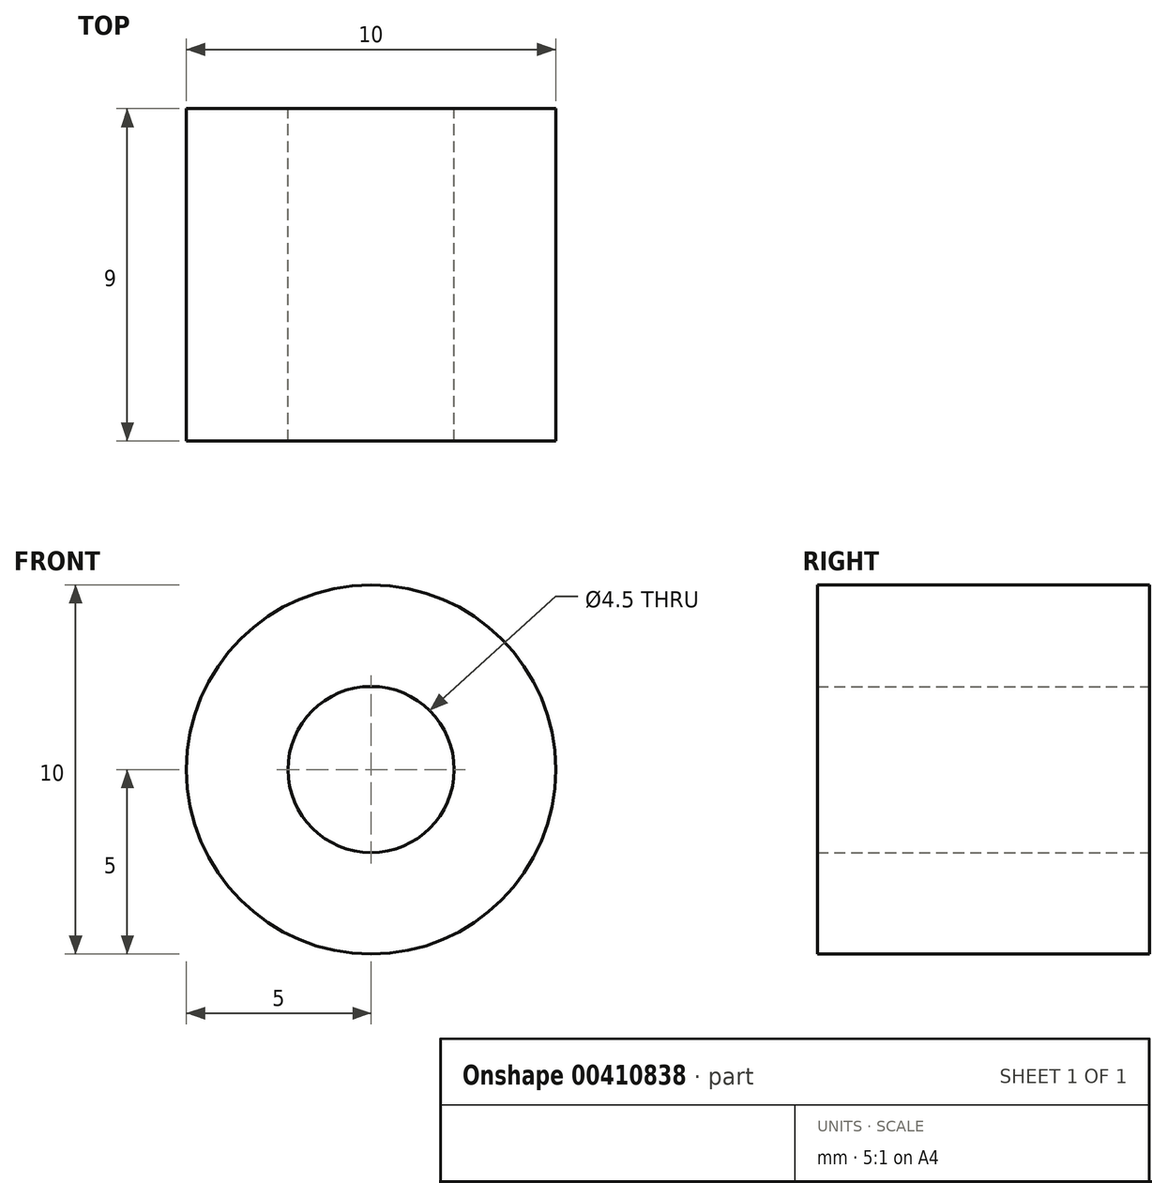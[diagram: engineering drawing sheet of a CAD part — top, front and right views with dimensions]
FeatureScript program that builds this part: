
annotation { "Feature Type Name" : "Feature", "Feature Type Description" : "" }
export const myFeature = defineFeature(function(context is Context, id is Id, definition is map)
    precondition{}
    {
        {
            var Q0;
            Q0=qCreatedBy(makeId("Front.planeOp"),FACE);
            var sketch = newSketch(context, id + "F0", { "sketchPlane" : qUnion([Q0])});
            skCircle(sketch, "E0", {"center": v(0, 0) * mm, "radius": 2.25 * mm});
            skCircle(sketch, "E1", {"center": v(0, 0) * mm, "radius": 5 * mm});
            skSolve(sketch);
        }
        {
            var Q0;
            Q0 = qSketchRegion(id + "F0", true);
            extrude(context, id + "F1", {"entities" : qUnion([Q0]), "depth" : 9 * mm});
        }
    });
